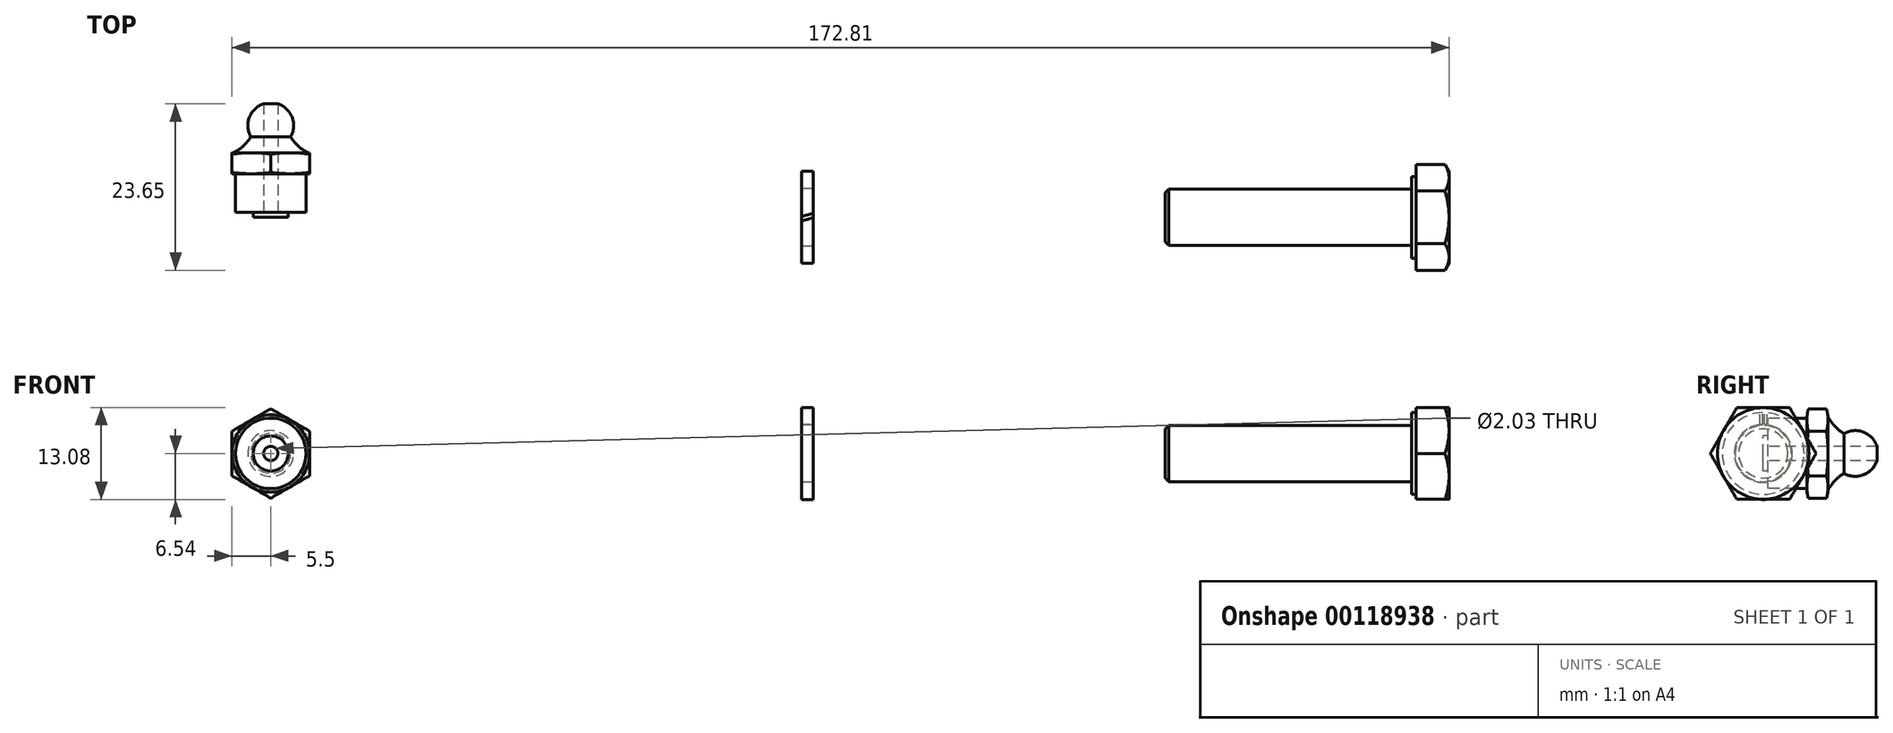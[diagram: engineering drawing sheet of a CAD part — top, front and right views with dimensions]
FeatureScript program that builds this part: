
annotation { "Feature Type Name" : "Feature", "Feature Type Description" : "" }
export const myFeature = defineFeature(function(context is Context, id is Id, definition is map)
    precondition{}
    {
        {
            var Q0;
            Q0=qCreatedBy(makeId("Right.planeOp"),FACE);
            cPlane(context, id + "F0", {"entities" : qUnion([Q0]), "cplaneType" : CPlaneType.OFFSET, "offset" : 152.4 * mm, "width" : 152.4 * mm, "height" : 152.4 * mm});
        }
        {
            var Q0;
            Q0=qCreatedBy(id+"F0.planeOp",FACE);
            var sketch = newSketch(context, id + "F1", { "sketchPlane" : qUnion([Q0])});
            skLineSegment(sketch, "E0", {"start": v(0, 0) * mm, "end": v(0, 2.49) * mm});
            skLineSegment(sketch, "E1", {"start": v(0, 2.49) * mm, "end": v(0.71, 2.49) * mm});
            skLineSegment(sketch, "E2", {"start": v(0.71, 2.49) * mm, "end": v(0.71, 5) * mm});
            skLineSegment(sketch, "E3", {"start": v(0.71, 5) * mm, "end": v(6.2, 5) * mm});
            skLineSegment(sketch, "E4", {"start": v(6.2, 5) * mm, "end": v(6.2, 5.26) * mm});
            skLineSegment(sketch, "E5", {"start": v(6.2, 5.26) * mm, "end": v(9.2, 5.26) * mm});
            skArc(sketch, "E6", {"start": v(9.2, 5.26) * mm, "mid": v(10.15, 3.88) * mm, "end": v(11.45, 2.83) * mm});
            skArc(sketch, "E7", {"start": v(16.3, 0) * mm, "mid": v(14.7, 2.8) * mm, "end": v(11.45, 2.83) * mm});
            skLineSegment(sketch, "E8", {"start": v(0, 0) * mm, "end": v(16.3, 0) * mm});
            skPoint(sketch, "E9.orphan", {"position": v(11.79, 2.64) * mm});
            skSolve(sketch);
        }
        {
            var Q0;
            Q0=makeQuery(id+"F1.imprint","IMPRINT",FACE,{"disambiguationData":[TD([[makeQuery(id+"F1.imprint","IMPRINT",EDGE,{"derivedFrom":sQuery(id+"F1.wireOp",EDGE,"E0")}),-1.0]])]});
            var Q1;
            Q1=sQuery(id+"F1.wireOp",EDGE,"E8");
            revolve(context, id + "F2", {"entities" : qUnion([Q0]), "axis" : qUnion([Q1]), "revolveType" : RevolveType.FULL});
        }
        {
            var Q0;
            Q0=makeQuery(id+"F2.opRevolve","SWEPT_FACE",FACE,{"disambiguationData":[OSD([sQuery(id+"F1.wireOp",EDGE,"E0")])]});
            cPlane(context, id + "F3", {"entities" : qUnion([Q0]), "cplaneType" : CPlaneType.OFFSET, "offset" : 6.2 * mm, "oppositeDirection" : true, "width" : 152.4 * mm, "height" : 152.4 * mm});
        }
        {
            var Q0;
            Q0=qCreatedBy(id+"F3.planeOp",FACE);
            var sketch = newSketch(context, id + "F4", { "sketchPlane" : qUnion([Q0])});
            skPoint(sketch, "E10", {"position": v(152.4, 0) * mm});
            skLineSegment(sketch, "E11", {"start": v(152.4, 0) * mm, "end": v(159.09, 0) * mm, "construction": true});
            skLineSegment(sketch, "E12.0", {"start": v(152.4, -3.18) * mm, "end": v(159.09, -3.18) * mm, "construction": true});
            skLineSegment(sketch, "E13.0", {"start": v(152.4, 3.18) * mm, "end": v(157.9, 3.18) * mm, "construction": true});
            skCircle(sketch, "E14", {"center": v(152.4, 0) * mm, "radius": 5.5 * mm, "construction": true});
            skLineSegment(sketch, "E15", {"start": v(157.9, 3.18) * mm, "end": v(157.9, -3.18) * mm});
            skLineSegment(sketch, "E16", {"start": v(152.4, 7.44) * mm, "end": v(152.4, -7.15) * mm, "construction": true});
            skLineSegment(sketch, "E17.0.MirrorCS", {"start": v(146.9, 3.17) * mm, "end": v(146.9, -3.18) * mm});
            skLineSegment(sketch, "E18", {"start": v(157.9, 3.18) * mm, "end": v(152.4, 6.35) * mm});
            skLineSegment(sketch, "E19.0.MirrorCS", {"start": v(157.9, -3.18) * mm, "end": v(152.4, -6.35) * mm});
            skLineSegment(sketch, "E20.0.MirrorCS", {"start": v(146.9, -3.18) * mm, "end": v(152.4, -6.35) * mm});
            skLineSegment(sketch, "E21", {"start": v(152.4, 6.35) * mm, "end": v(146.9, 3.17) * mm});
            skSolve(sketch);
        }
        {
            var Q0;
            {var subQ4=sQuery(id+"F4.wireOp",EDGE,"E15");Q0=makeQuery(id+"F4.imprint","IMPRINT",FACE,{"disambiguationData":[TD([[makeQuery(id+"F4.imprint","IMPRINT",EDGE,{"derivedFrom":subQ4}),-1.0]])]});}
            extrude(context, id + "F5", {"entities" : qUnion([Q0]), "operationType" : NewBodyOperationType.ADD, "oppositeDirection" : true, "depth" : 3 * mm});
        }
        {
            var Q0;
            Q0=makeQuery(id+"F5.opExtrude","SWEPT_FACE",FACE,{"disambiguationData":[OSD([sQuery(id+"F4.wireOp",EDGE,"E21")])]});
            cPlane(context, id + "F6", {"entities" : qUnion([Q0]), "cplaneType" : CPlaneType.OFFSET, "offset" : 5.5 * mm, "oppositeDirection" : true, "width" : 152.4 * mm, "height" : 152.4 * mm});
        }
        {
            var Q0;
            Q0=qCreatedBy(id+"F6.planeOp",FACE);
            var sketch = newSketch(context, id + "F7", { "sketchPlane" : qUnion([Q0])});
            skLineSegment(sketch, "E22.0", {"start": v(138.33, 6.2) * mm, "end": v(137.48, 6.2) * mm});
            skLineSegment(sketch, "E23", {"start": v(139.63, 7.7) * mm, "end": v(134.5, 7.7) * mm, "construction": true});
            skPoint(sketch, "E24.orphan", {"position": v(135.16, 9.2) * mm});
            skLineSegment(sketch, "E25.0.MirrorCS", {"start": v(137.77, 6.2) * mm, "end": v(138.33, 6.2) * mm});
            skLineSegment(sketch, "E26", {"start": v(138.33, 6.2) * mm, "end": v(137.77, 6.2) * mm});
            skLineSegment(sketch, "E27.0", {"start": v(137.48, 6.2) * mm, "end": v(126.48, 6.2) * mm});
            skLineSegment(sketch, "E28", {"start": v(137.48, 6.2) * mm, "end": v(138.33, 6.4) * mm});
            skPoint(sketch, "E29.orphan", {"position": v(135.16, 6.2) * mm});
            skLineSegment(sketch, "E30", {"start": v(138.33, 6.4) * mm, "end": v(138.33, 6.2) * mm});
            skLineSegment(sketch, "E31", {"start": v(137.48, 6.2) * mm, "end": v(138.33, 6.2) * mm});
            skLineSegment(sketch, "E32.0.MirrorCS", {"start": v(137.48, 9.2) * mm, "end": v(138.33, 9) * mm});
            skLineSegment(sketch, "E33.0.MirrorCS", {"start": v(138.33, 9) * mm, "end": v(138.33, 9.2) * mm});
            skLineSegment(sketch, "E34.0.MirrorCS", {"start": v(138.33, 9.2) * mm, "end": v(137.48, 9.2) * mm});
            skSolve(sketch);
        }
        {
            var Q0;
            {var subQ4=sQuery(id+"F7.wireOp",EDGE,"E28");Q0=makeQuery(id+"F7.imprint","IMPRINT",FACE,{"disambiguationData":[TD([[makeQuery(id+"F7.imprint","IMPRINT",EDGE,{"derivedFrom":subQ4}),-1.0]])]});}
            var Q1;
            Q1=makeQuery(id+"F7.imprint","IMPRINT",FACE,{"disambiguationData":[TD([[makeQuery(id+"F7.imprint","IMPRINT",EDGE,{"derivedFrom":sQuery(id+"F7.wireOp",EDGE,"E32.0.MirrorCS")}),1.0]])]});
            var Q2;
            Q2=sQuery(id+"F4.wireOp",EDGE,"E14");
            revolve(context, id + "F8", {"operationType" : NewBodyOperationType.REMOVE, "entities" : qUnion([Q0, Q1]), "axis" : qUnion([Q2]), "revolveType" : RevolveType.FULL, "oppositeDirection" : true});
        }
        {
            var Q0;
            Q0=qCreatedBy(id+"F3.planeOp",FACE);
            var sketch = newSketch(context, id + "F9", { "sketchPlane" : qUnion([Q0])});
            skCircle(sketch, "E35", {"center": v(152.4, 0) * mm, "radius": 1.02 * mm});
            skSolve(sketch);
        }
        {
            var Q0;
            Q0=makeQuery(id+"F9.imprint","IMPRINT",FACE,{"disambiguationData":[TD([[makeQuery(id+"F9.imprint","IMPRINT",EDGE,{"derivedFrom":sQuery(id+"F9.wireOp",EDGE,"E35")}),1.0]])]});
            var Q1;
            Q1=makeQuery(id+"F2.opRevolve","SWEPT_FACE",FACE,{"disambiguationData":[OSD([sQuery(id+"F1.wireOp",EDGE,"E7")])]});
            extrude(context, id + "F10", {"entities" : qUnion([Q0]), "operationType" : NewBodyOperationType.REMOVE, "endBound" : BoundingType.SYMMETRIC, "oppositeDirection" : true, "endBoundEntity" : qUnion([Q1]), "depth" : 25.4 * mm});
        }
        {
            var Q0;
            Q0=qCreatedBy(id+"F0.planeOp",FACE);
            cPlane(context, id + "F11", {"entities" : qUnion([Q0]), "cplaneType" : CPlaneType.OFFSET, "offset" : 76.2 * mm, "width" : 152.4 * mm, "height" : 152.4 * mm});
        }
        {
            var Q0;
            Q0=qCreatedBy(id+"F11.planeOp",FACE);
            var sketch = newSketch(context, id + "F12", { "sketchPlane" : qUnion([Q0])});
            skCircle(sketch, "E36", {"center": v(0, 0) * mm, "radius": 6.54 * mm});
            skCircle(sketch, "E37", {"center": v(0, 0) * mm, "radius": 4.1 * mm});
            skSolve(sketch);
        }
        {
            var Q0;
            Q0=makeQuery(id+"F12.imprint","IMPRINT",FACE,{"disambiguationData":[TD([[makeQuery(id+"F12.imprint","IMPRINT",EDGE,{"derivedFrom":sQuery(id+"F12.wireOp",EDGE,"E36")}),1.0]])]});
            extrude(context, id + "F13", {"entities" : qUnion([Q0]), "endBound" : BoundingType.SYMMETRIC, "depth" : 1.6 * mm});
        }
        {
            var Q0;
            Q0=qCreatedBy(makeId("Top.planeOp"),FACE);
            cPlane(context, id + "F14", {"entities" : qUnion([Q0]), "cplaneType" : CPlaneType.OFFSET, "offset" : 5.08 * mm, "width" : 152.4 * mm, "height" : 152.4 * mm});
        }
        {
            var Q0;
            Q0=qCreatedBy(id+"F14.planeOp",FACE);
            var sketch = newSketch(context, id + "F15", { "sketchPlane" : qUnion([Q0])});
            skLineSegment(sketch, "E38", {"start": v(0, 0) * mm, "end": v(259.22, 0) * mm, "construction": true});
            skLineSegment(sketch, "E39", {"start": v(229.4, -0.06) * mm, "end": v(227.8, -0.49) * mm});
            skLineSegment(sketch, "E40", {"start": v(227.8, 0.14) * mm, "end": v(229.4, 0.57) * mm});
            skLineSegment(sketch, "E41.0", {"start": v(227.8, 0.14) * mm, "end": v(227.8, -0.49) * mm});
            skPoint(sketch, "E42.orphan", {"position": v(227.8, -6.54) * mm});
            skLineSegment(sketch, "E43.1", {"start": v(229.4, 0.57) * mm, "end": v(229.4, -0.06) * mm});
            skPoint(sketch, "E44.orphan", {"position": v(229.4, 6.54) * mm});
            skPoint(sketch, "E45.orphan", {"position": v(229.4, -6.54) * mm});
            skPoint(sketch, "E46.orphan", {"position": v(227.8, 6.54) * mm});
            skSolve(sketch);
        }
        {
            var Q0;
            Q0=makeQuery(id+"F15.imprint","IMPRINT",FACE,{"disambiguationData":[TD([[makeQuery(id+"F15.imprint","IMPRINT",EDGE,{"derivedFrom":sQuery(id+"F15.wireOp",EDGE,"E39")}),-1.0]])]});
            extrude(context, id + "F16", {"entities" : qUnion([Q0]), "operationType" : NewBodyOperationType.REMOVE, "endBound" : BoundingType.SYMMETRIC, "oppositeDirection" : true, "depth" : 12.7 * mm});
        }
        {
            var Q0;
            Q0=qCreatedBy(id+"F11.planeOp",FACE);
            cPlane(context, id + "F17", {"entities" : qUnion([Q0]), "cplaneType" : CPlaneType.OFFSET, "offset" : 50.8 * mm, "width" : 152.4 * mm, "height" : 152.4 * mm});
        }
        {
            var Q0;
            Q0=qCreatedBy(id+"F17.planeOp",FACE);
            var sketch = newSketch(context, id + "F18", { "sketchPlane" : qUnion([Q0])});
            skCircle(sketch, "E47", {"center": v(0, 0) * mm, "radius": 4 * mm});
            skSolve(sketch);
        }
        {
            var Q0;
            Q0=makeQuery(id+"F18.imprint","IMPRINT",FACE,{"disambiguationData":[TD([[makeQuery(id+"F18.imprint","IMPRINT",EDGE,{"derivedFrom":sQuery(id+"F18.wireOp",EDGE,"E47")}),1.0]])]});
            extrude(context, id + "F19", {"entities" : qUnion([Q0]), "depth" : 35 * mm});
        }
        {
            var Q0;
            Q0=makeQuery(id+"F19.opExtrude","CAP_FACE",FACE,{"disambiguationData":[OSD([sQuery(id+"F18.wireOp",EDGE,"E47")])],"isStart":false});
            var sketch = newSketch(context, id + "F20", { "sketchPlane" : qUnion([Q0])});
            skCircle(sketch, "E48", {"center": v(0, 0) * mm, "radius": 5.82 * mm});
            skSolve(sketch);
        }
        {
            var Q0;
            {var subQ0=makeQuery(id+"F20.imprint","IMPRINT",EDGE,{"derivedFrom":makeQuery(id+"F19.opExtrude","CAP_EDGE",EDGE,{"disambiguationData":[OSD([sQuery(id+"F18.wireOp",EDGE,"E47")])],"isStart":false})});Q0=qUnion([makeQuery(id+"F20.imprint","IMPRINT",FACE,{"disambiguationData":[TD([[makeQuery(id+"F20.imprint","IMPRINT",EDGE,{"derivedFrom":sQuery(id+"F20.wireOp",EDGE,"E48")}),1.0]])]}),makeQuery(id+"F20.imprint","IMPRINT",FACE,{"disambiguationData":[TD([[subQ0,1.0]])]})]);}
            extrude(context, id + "F21", {"entities" : qUnion([Q0]), "operationType" : NewBodyOperationType.ADD, "depth" : 0.6 * mm});
        }
        {
            var Q0;
            Q0=makeQuery(id+"F21.opExtrude","CAP_FACE",FACE,{"disambiguationData":[OSD([sQuery(id+"F20.wireOp",EDGE,"E48")])],"isStart":false});
            var sketch = newSketch(context, id + "F22", { "sketchPlane" : qUnion([Q0])});
            skCircle(sketch, "E49", {"center": v(0, 0) * mm, "radius": 6.5 * mm, "construction": true});
            skLineSegment(sketch, "E50", {"start": v(0, 0) * mm, "end": v(0, 8.78) * mm, "construction": true});
            skLineSegment(sketch, "E51", {"start": v(0, 0) * mm, "end": v(-8.38, 0) * mm, "construction": true});
            skLineSegment(sketch, "E52", {"start": v(-3.75, 6.5) * mm, "end": v(3.75, 6.5) * mm});
            skLineSegment(sketch, "E53", {"start": v(-3.75, 6.5) * mm, "end": v(-7.5, 0) * mm});
            skLineSegment(sketch, "E54.0.MirrorCS", {"start": v(3.75, 6.5) * mm, "end": v(7.5, 0) * mm});
            skLineSegment(sketch, "E55.0.MirrorCS", {"start": v(-3.75, -6.5) * mm, "end": v(-7.5, 0) * mm});
            skLineSegment(sketch, "E56.0.MirrorCS", {"start": v(3.75, -6.5) * mm, "end": v(7.5, 0) * mm});
            skLineSegment(sketch, "E57.0.MirrorCS", {"start": v(-3.75, -6.5) * mm, "end": v(3.75, -6.5) * mm});
            skSolve(sketch);
        }
        {
            var Q0;
            {var subQ0=makeQuery(id+"F22.imprint","IMPRINT",EDGE,{"derivedFrom":makeQuery(id+"F21.opExtrude","CAP_EDGE",EDGE,{"disambiguationData":[OSD([sQuery(id+"F20.wireOp",EDGE,"E48")])],"isStart":false})});Q0=qUnion([makeQuery(id+"F22.imprint","IMPRINT",FACE,{"disambiguationData":[TD([[makeQuery(id+"F22.imprint","IMPRINT",EDGE,{"derivedFrom":sQuery(id+"F22.wireOp",EDGE,"E52")}),-1.0]])]}),makeQuery(id+"F22.imprint","IMPRINT",FACE,{"disambiguationData":[TD([[subQ0,1.0]])]})]);}
            var Q1;
            Q1=sQuery(id+"F22.wireOp",EDGE,"E52");
            extrude(context, id + "F23", {"entities" : qUnion([Q0]), "operationType" : NewBodyOperationType.ADD, "surfaceEntities" : qUnion([Q1]), "depth" : 4.7 * mm});
        }
        {
            var Q0;
            Q0=makeQuery(id+"F23.opExtrude","SWEPT_FACE",FACE,{"disambiguationData":[OSD([sQuery(id+"F22.wireOp",EDGE,"E55.0.MirrorCS")])]});
            cPlane(context, id + "F24", {"entities" : qUnion([Q0]), "cplaneType" : CPlaneType.OFFSET, "offset" : 6.5 * mm, "oppositeDirection" : true, "width" : 152.4 * mm, "height" : 152.4 * mm});
        }
        {
            var Q0;
            Q0=qCreatedBy(id+"F24.planeOp",FACE);
            var sketch = newSketch(context, id + "F25", { "sketchPlane" : qUnion([Q0])});
            skPoint(sketch, "E58", {"position": v(319.7, 6.5) * mm});
            skLineSegment(sketch, "E59", {"start": v(319.7, 6.5) * mm, "end": v(319.7, 7.5) * mm});
            skLineSegment(sketch, "E60.0", {"start": v(319.7, 7.5) * mm, "end": v(319.13, 7.5) * mm});
            skLineSegment(sketch, "E61", {"start": v(319.7, 6.5) * mm, "end": v(319.13, 7.5) * mm});
            skPoint(sketch, "E62.orphan", {"position": v(315.01, 7.5) * mm});
            skSolve(sketch);
        }
        {
            var Q0;
            Q0=makeQuery(id+"F25.imprint","IMPRINT",FACE,{"disambiguationData":[TD([[makeQuery(id+"F25.imprint","IMPRINT",EDGE,{"derivedFrom":sQuery(id+"F25.wireOp",EDGE,"E59")}),1.0]])]});
            var Q1;
            Q1=sQuery(id+"F22.wireOp",EDGE,"E49");
            revolve(context, id + "F26", {"operationType" : NewBodyOperationType.REMOVE, "entities" : qUnion([Q0]), "axis" : qUnion([Q1]), "revolveType" : RevolveType.FULL, "oppositeDirection" : true});
        }
        {
            var Q0;
            Q0=makeQuery(id+"F19.opExtrude","CAP_EDGE",EDGE,{"disambiguationData":[OSD([sQuery(id+"F18.wireOp",EDGE,"E47")])],"isStart":true});
            chamfer(context, id + "F27", {"entities" : qUnion([Q0]), "width" : 0.5 * mm, "tangentPropagation" : true});
        }
    });
